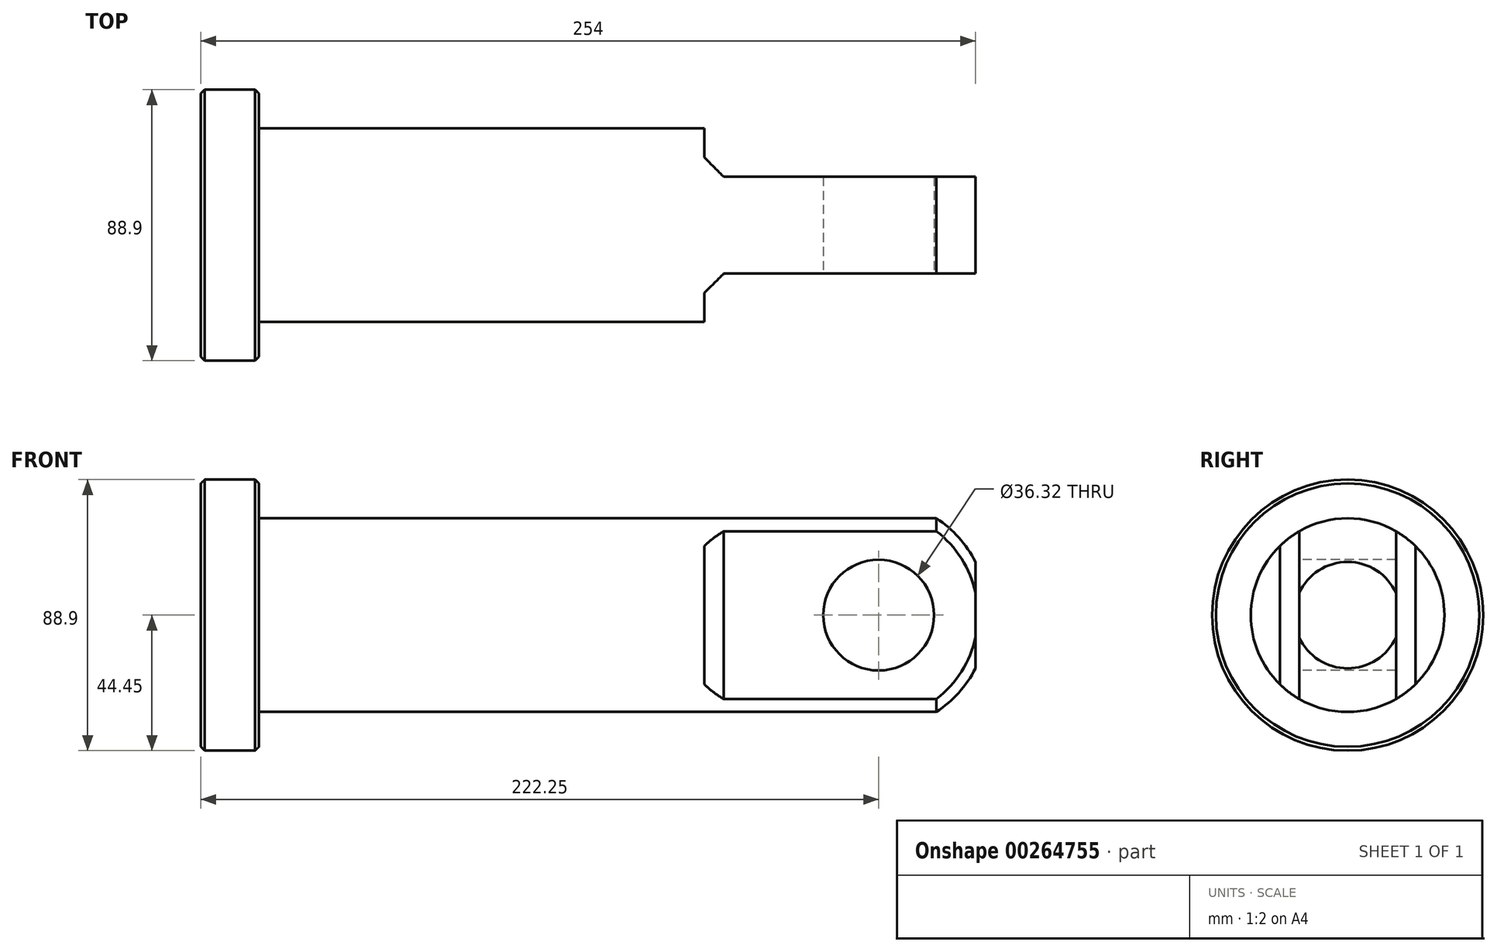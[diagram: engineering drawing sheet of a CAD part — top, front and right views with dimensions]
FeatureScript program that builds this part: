
annotation { "Feature Type Name" : "Feature", "Feature Type Description" : "" }
export const myFeature = defineFeature(function(context is Context, id is Id, definition is map)
    precondition{}
    {
        {
            var Q0;
            Q0=qCreatedBy(makeId("Front.planeOp"),FACE);
            var sketch = newSketch(context, id + "F0", { "sketchPlane" : qUnion([Q0])});
            skLineSegment(sketch, "E0", {"start": v(0, 0) * mm, "end": v(0, 17.46) * mm});
            skLineSegment(sketch, "E1", {"start": v(-12.8, 31.75) * mm, "end": v(-234.95, 31.75) * mm});
            skLineSegment(sketch, "E2", {"start": v(-234.95, 31.75) * mm, "end": v(-234.95, 44.45) * mm});
            skLineSegment(sketch, "E3", {"start": v(-234.95, 44.45) * mm, "end": v(-254, 44.45) * mm});
            skLineSegment(sketch, "E4", {"start": v(-254, 44.45) * mm, "end": v(-254, 0) * mm});
            skLineSegment(sketch, "E5", {"start": v(-254, 0) * mm, "end": v(0, 0) * mm});
            skLineSegment(sketch, "E6", {"start": v(20.48, 0) * mm, "end": v(-272.1, 0) * mm, "construction": true});
            skArc(sketch, "E7", {"start": v(0, 17.46) * mm, "mid": v(-5.49, 25.43) * mm, "end": v(-12.8, 31.75) * mm});
            skSolve(sketch);
        }
        {
            var Q0;
            Q0=makeQuery(id+"F0.imprint","IMPRINT",FACE,{"disambiguationData":[TD([[makeQuery(id+"F0.imprint","IMPRINT",EDGE,{"derivedFrom":sQuery(id+"F0.wireOp",EDGE,"E0")}),1.0]])]});
            var Q1;
            Q1=sQuery(id+"F0.wireOp",EDGE,"E6");
            revolve(context, id + "F1", {"entities" : qUnion([Q0]), "axis" : qUnion([Q1]), "revolveType" : RevolveType.FULL});
        }
        {
            var Q0;
            Q0=qCreatedBy(makeId("Top.planeOp"),FACE);
            var sketch = newSketch(context, id + "F2", { "sketchPlane" : qUnion([Q0])});
            skLineSegment(sketch, "E8.bottom", {"start": v(0, 15.87) * mm, "end": v(-88.9, 15.87) * mm});
            skLineSegment(sketch, "E8.top", {"start": v(0, 31.75) * mm, "end": v(-88.9, 31.75) * mm});
            skLineSegment(sketch, "E8.left", {"start": v(0, 15.87) * mm, "end": v(0, 31.75) * mm});
            skLineSegment(sketch, "E8.right", {"start": v(-88.9, 15.87) * mm, "end": v(-88.9, 31.75) * mm});
            skLineSegment(sketch, "E9.MirrorCS", {"start": v(0, -31.75) * mm, "end": v(-88.9, -31.75) * mm});
            skLineSegment(sketch, "E10.MirrorCS", {"start": v(0, -15.87) * mm, "end": v(0, -31.75) * mm});
            skLineSegment(sketch, "E11.MirrorCS", {"start": v(0, -15.87) * mm, "end": v(-88.9, -15.87) * mm});
            skLineSegment(sketch, "E12.MirrorCS", {"start": v(-88.9, -15.87) * mm, "end": v(-88.9, -31.75) * mm});
            skSolve(sketch);
        }
        {
            var Q0;
            Q0=makeQuery(id+"F2.imprint","IMPRINT",FACE,{"disambiguationData":[TD([[makeQuery(id+"F2.imprint","IMPRINT",EDGE,{"derivedFrom":sQuery(id+"F2.wireOp",EDGE,"E8.bottom")}),-1.0]])]});
            var Q1;
            Q1=makeQuery(id+"F2.imprint","IMPRINT",FACE,{"disambiguationData":[TD([[makeQuery(id+"F2.imprint","IMPRINT",EDGE,{"derivedFrom":sQuery(id+"F2.wireOp",EDGE,"E9.MirrorCS")}),-1.0]])]});
            extrude(context, id + "F3", {"entities" : qUnion([Q0, Q1]), "operationType" : NewBodyOperationType.REMOVE, "endBound" : BoundingType.SYMMETRIC, "oppositeDirection" : true, "depth" : 63.5 * mm});
        }
        {
            var Q0;
            Q0=makeQuery(id+"F3.boolean.opBoolean","COPY",EDGE,{"derivedFrom":makeQuery(id+"F3.opExtrude","SWEPT_EDGE",EDGE,{"disambiguationData":[OSD([sQuery(id+"F2.wireOp",EDGE,"E11.MirrorCS"),sQuery(id+"F2.wireOp",EDGE,"E12.MirrorCS")])]})});
            var Q1;
            Q1=makeQuery(id+"F3.boolean.opBoolean","COPY",EDGE,{"derivedFrom":makeQuery(id+"F3.opExtrude","SWEPT_EDGE",EDGE,{"disambiguationData":[OSD([sQuery(id+"F2.wireOp",EDGE,"E8.bottom"),sQuery(id+"F2.wireOp",EDGE,"E8.right")])]})});
            chamfer(context, id + "F4", {"entities" : qUnion([Q0, Q1]), "width" : 6.35 * mm, "tangentPropagation" : true});
        }
        {
            var Q0;
            Q0=makeQuery(id+"F3.boolean.opBoolean","COPY",FACE,{"derivedFrom":makeQuery(id+"F3.opExtrude","SWEPT_FACE",FACE,{"disambiguationData":[OSD([sQuery(id+"F2.wireOp",EDGE,"E11.MirrorCS")])]})});
            var sketch = newSketch(context, id + "F5", { "sketchPlane" : qUnion([Q0])});
            skCircle(sketch, "E13", {"center": v(-31.75, 0) * mm, "radius": 18.16 * mm});
            skSolve(sketch);
        }
        {
            var Q0;
            Q0=makeQuery(id+"F5.imprint","IMPRINT",FACE,{"disambiguationData":[TD([[makeQuery(id+"F5.imprint","IMPRINT",EDGE,{"derivedFrom":sQuery(id+"F5.wireOp",EDGE,"E13")}),1.0]])]});
            extrude(context, id + "F6", {"entities" : qUnion([Q0]), "operationType" : NewBodyOperationType.REMOVE, "endBound" : BoundingType.THROUGH_ALL, "oppositeDirection" : true, "depth" : 25.4 * mm});
        }
        {
            var Q0;
            Q0=makeQuery(id+"F1.opRevolve","SWEPT_EDGE",EDGE,{"disambiguationData":[OSD([sQuery(id+"F0.wireOp",EDGE,"E2"),sQuery(id+"F0.wireOp",EDGE,"E3")])]});
            var Q1;
            Q1=makeQuery(id+"F1.opRevolve","SWEPT_EDGE",EDGE,{"disambiguationData":[OSD([sQuery(id+"F0.wireOp",EDGE,"E3"),sQuery(id+"F0.wireOp",EDGE,"E4")])]});
            chamfer(context, id + "F7", {"entities" : qUnion([Q0, Q1]), "width" : 1.27 * mm, "tangentPropagation" : true});
        }
    });
